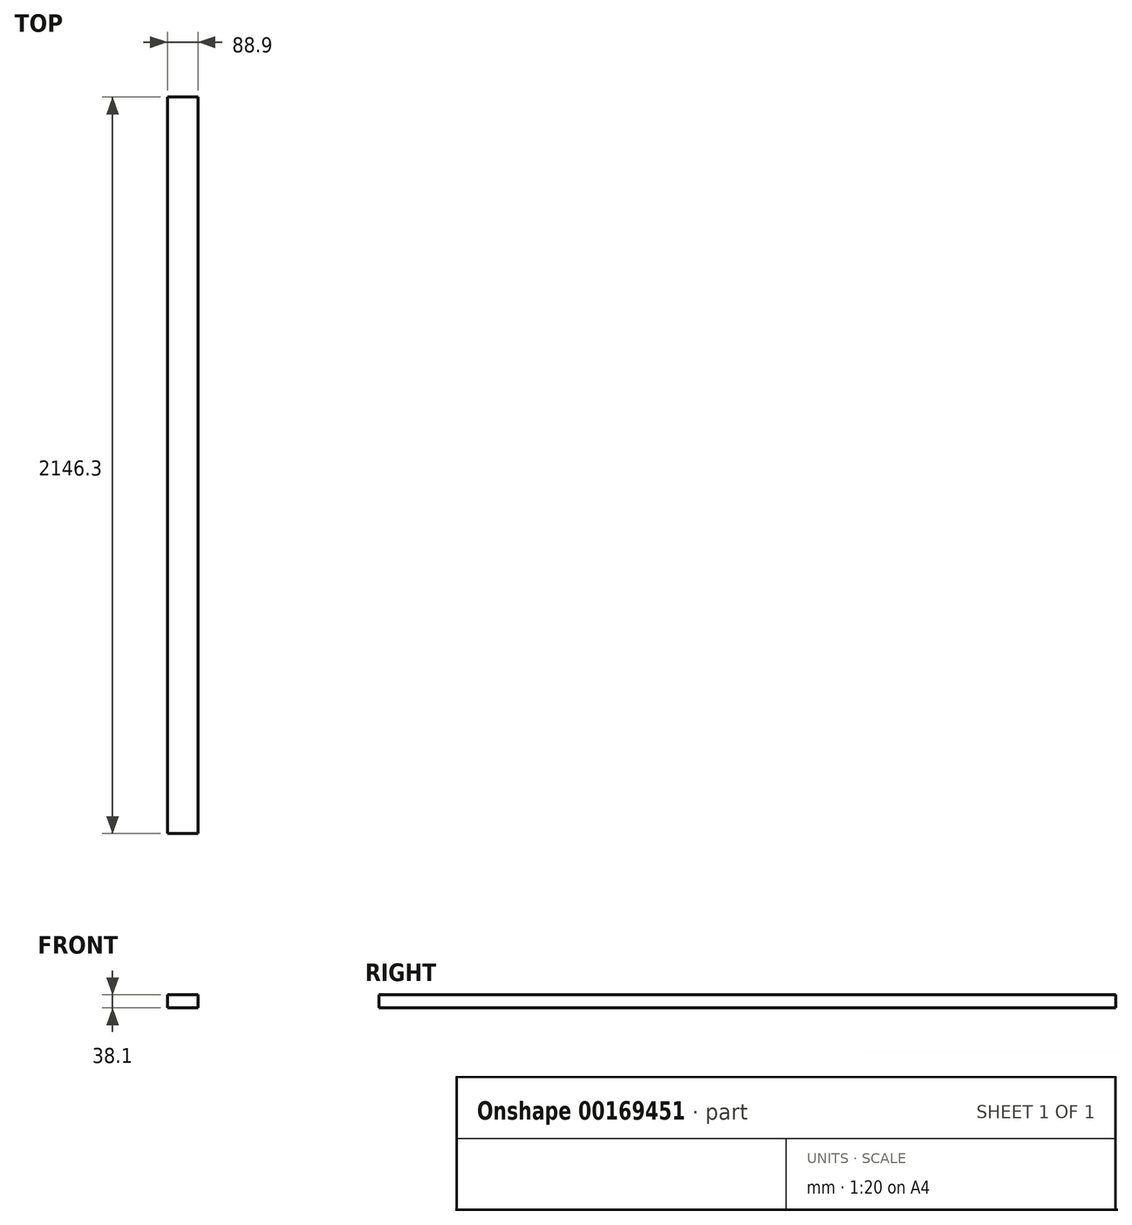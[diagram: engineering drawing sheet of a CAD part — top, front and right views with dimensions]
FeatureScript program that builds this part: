
annotation { "Feature Type Name" : "Feature", "Feature Type Description" : "" }
export const myFeature = defineFeature(function(context is Context, id is Id, definition is map)
    precondition{}
    {
        {
            var Q0;
            Q0=qCreatedBy(makeId("Front.planeOp"),FACE);
            var sketch = newSketch(context, id + "F0", { "sketchPlane" : qUnion([Q0])});
            skLineSegment(sketch, "E0.bottom", {"start": v(0, 0) * mm, "end": v(88.9, 0) * mm});
            skLineSegment(sketch, "E0.top", {"start": v(0, -38.1) * mm, "end": v(88.9, -38.1) * mm});
            skLineSegment(sketch, "E0.left", {"start": v(0, 0) * mm, "end": v(0, -38.1) * mm});
            skLineSegment(sketch, "E0.right", {"start": v(88.9, 0) * mm, "end": v(88.9, -38.1) * mm});
            skSolve(sketch);
        }
        {
            var Q0;
            Q0=qSketchRegion(id+"F0",true);
            extrude(context, id + "F1", {"entities" : qUnion([Q0]), "depth" : 2146.3 * mm});
        }
    });
